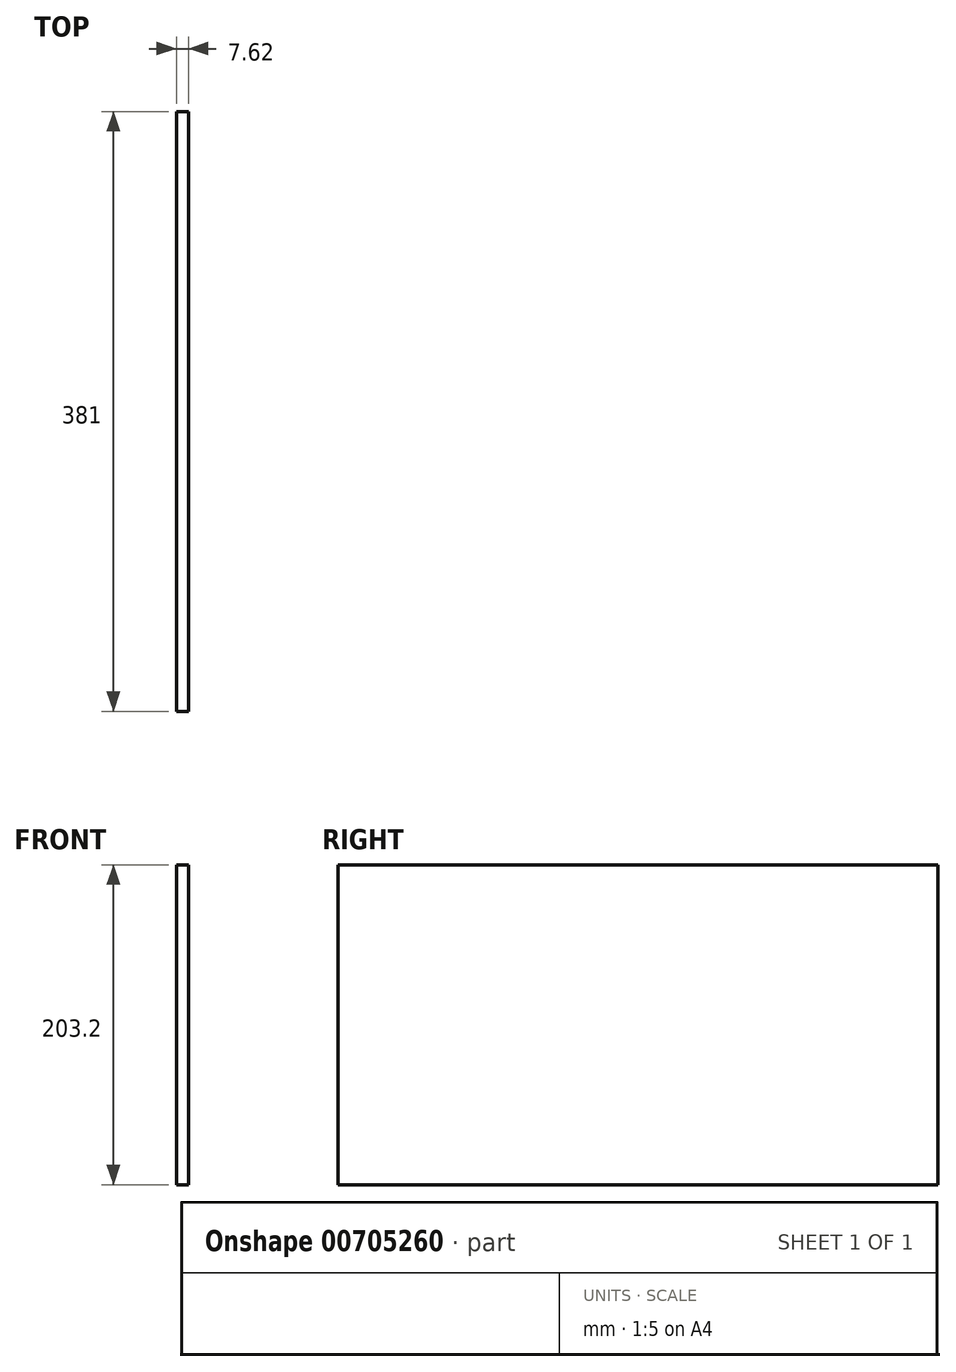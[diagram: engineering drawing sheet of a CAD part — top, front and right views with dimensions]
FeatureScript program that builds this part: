
annotation { "Feature Type Name" : "Feature", "Feature Type Description" : "" }
export const myFeature = defineFeature(function(context is Context, id is Id, definition is map)
    precondition{}
    {
        {
            var Q0;
            Q0=qCreatedBy(makeId("Right.planeOp"),FACE);
            var sketch = newSketch(context, id + "F0", { "sketchPlane" : qUnion([Q0])});
            skLineSegment(sketch, "E0.bottom", {"start": v(-184.47, 4.31) * mm, "end": v(196.53, 4.31) * mm});
            skLineSegment(sketch, "E0.top", {"start": v(-184.47, -198.89) * mm, "end": v(196.53, -198.89) * mm});
            skLineSegment(sketch, "E0.left", {"start": v(-184.47, 4.31) * mm, "end": v(-184.47, -198.89) * mm});
            skLineSegment(sketch, "E0.right", {"start": v(196.53, 4.31) * mm, "end": v(196.53, -198.89) * mm});
            skSolve(sketch);
        }
        {
            var Q0;
            Q0 = qSketchRegion(id + "F0", true);
            extrude(context, id + "F1", {"entities" : qUnion([Q0]), "depth" : 7.62 * mm, "offsetDistance" : 25.4 * mm});
        }
    });
